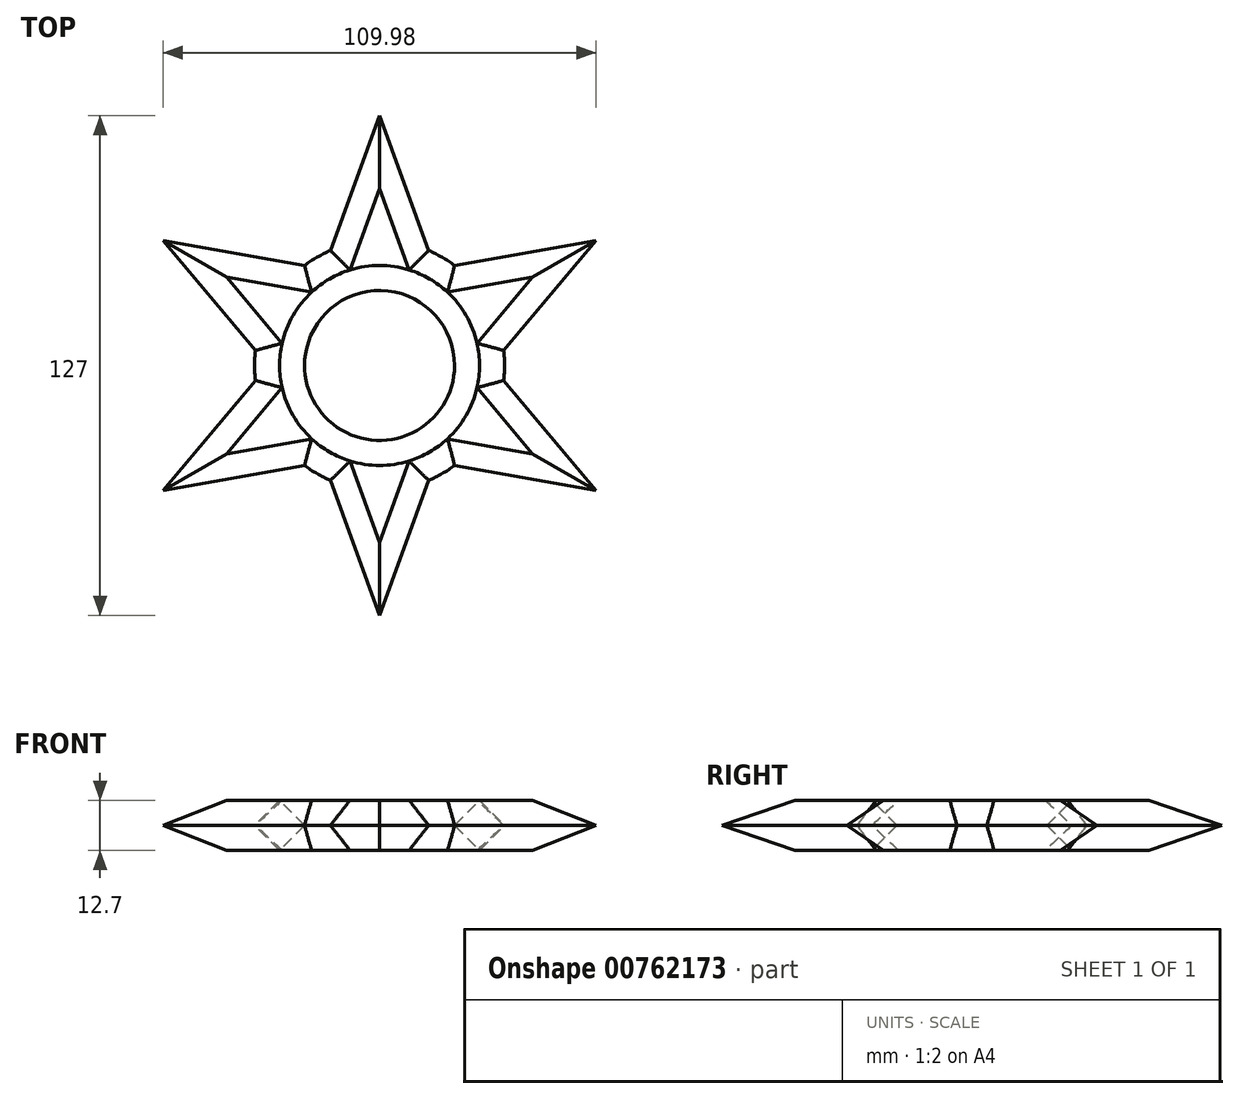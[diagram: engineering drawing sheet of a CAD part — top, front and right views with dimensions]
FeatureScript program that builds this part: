
annotation { "Feature Type Name" : "Feature", "Feature Type Description" : "" }
export const myFeature = defineFeature(function(context is Context, id is Id, definition is map)
    precondition{}
    {
        {
            var Q0;
            Q0=qCreatedBy(makeId("Top.planeOp"),FACE);
            var sketch = newSketch(context, id + "F0", { "sketchPlane" : qUnion([Q0])});
            skCircle(sketch, "E0", {"center": v(0, 0) * mm, "radius": 31.75 * mm});
            skCircle(sketch, "E1", {"center": v(0, 0) * mm, "radius": 19.05 * mm});
            skSolve(sketch);
        }
        {
            var Q0;
            Q0 = qSketchRegion(id + "F0", true);
            extrude(context, id + "F1", {"entities" : qUnion([Q0]), "endBound" : BoundingType.SYMMETRIC, "depth" : 12.7 * mm, "offsetDistance" : 25.4 * mm});
        }
        {
            var Q0;
            Q0=makeQuery(id+"F1.opExtrude","CAP_FACE",FACE,{"disambiguationData":[OSD([sQuery(id+"F0.wireOp",EDGE,"E0"),sQuery(id+"F0.wireOp",EDGE,"E1")])],"isStart":false});
            var sketch = newSketch(context, id + "F2", { "sketchPlane" : qUnion([Q0])});
            skLineSegment(sketch, "E2", {"start": v(0, 0) * mm, "end": v(0, 63.5) * mm});
            skCircle(sketch, "E3.0", {"center": v(0, 0) * mm, "radius": 31.75 * mm});
            skLineSegment(sketch, "E4", {"start": v(0, 63.5) * mm, "end": v(-12.49, 29.2) * mm});
            skLineSegment(sketch, "E5", {"start": v(0, 63.5) * mm, "end": v(12.49, 29.2) * mm});
            skLineSegment(sketch, "E6.1.0", {"start": v(-55, 31.75) * mm, "end": v(-31.52, 3.78) * mm});
            skLineSegment(sketch, "E6.1.1", {"start": v(-55, 31.75) * mm, "end": v(-19.04, 25.4) * mm});
            skLineSegment(sketch, "E6.2.0", {"start": v(-55, -31.75) * mm, "end": v(-19.04, -25.4) * mm});
            skLineSegment(sketch, "E6.2.1", {"start": v(-55, -31.75) * mm, "end": v(-31.52, -3.78) * mm});
            skLineSegment(sketch, "E6.3.0", {"start": v(0, -63.5) * mm, "end": v(12.49, -29.2) * mm});
            skLineSegment(sketch, "E6.3.1", {"start": v(0, -63.5) * mm, "end": v(-12.49, -29.2) * mm});
            skLineSegment(sketch, "E6.4.0", {"start": v(55, -31.75) * mm, "end": v(31.52, -3.78) * mm});
            skLineSegment(sketch, "E6.4.1", {"start": v(55, -31.75) * mm, "end": v(19.04, -25.4) * mm});
            skLineSegment(sketch, "E6.5.0", {"start": v(55, 31.75) * mm, "end": v(19.04, 25.4) * mm});
            skLineSegment(sketch, "E6.5.1", {"start": v(55, 31.75) * mm, "end": v(31.52, 3.78) * mm});
            skSolve(sketch);
        }
        {
            var Q0;
            {var subQ0=sQuery(id+"F2.wireOp",EDGE,"E4");Q0=makeQuery(id+"F2.imprint","IMPRINT",FACE,{"disambiguationData":[TD([[makeQuery(id+"F2.imprint","IMPRINT",EDGE,{"derivedFrom":subQ0}),1.0]])]});}
            var Q1;
            {var subQ0=sQuery(id+"F2.wireOp",EDGE,"E5");Q1=makeQuery(id+"F2.imprint","IMPRINT",FACE,{"disambiguationData":[TD([[makeQuery(id+"F2.imprint","IMPRINT",EDGE,{"derivedFrom":subQ0}),-1.0]])]});}
            var Q2;
            {var subQ0=sQuery(id+"F2.wireOp",EDGE,"E6.5.0");Q2=makeQuery(id+"F2.imprint","IMPRINT",FACE,{"disambiguationData":[TD([[makeQuery(id+"F2.imprint","IMPRINT",EDGE,{"derivedFrom":subQ0}),1.0]])]});}
            var Q3;
            {var subQ0=sQuery(id+"F2.wireOp",EDGE,"E6.1.0");Q3=makeQuery(id+"F2.imprint","IMPRINT",FACE,{"disambiguationData":[TD([[makeQuery(id+"F2.imprint","IMPRINT",EDGE,{"derivedFrom":subQ0}),1.0]])]});}
            var Q4;
            {var subQ0=sQuery(id+"F2.wireOp",EDGE,"E6.2.0");Q4=makeQuery(id+"F2.imprint","IMPRINT",FACE,{"disambiguationData":[TD([[makeQuery(id+"F2.imprint","IMPRINT",EDGE,{"derivedFrom":subQ0}),1.0]])]});}
            var Q5;
            {var subQ0=sQuery(id+"F2.wireOp",EDGE,"E6.4.0");Q5=makeQuery(id+"F2.imprint","IMPRINT",FACE,{"disambiguationData":[TD([[makeQuery(id+"F2.imprint","IMPRINT",EDGE,{"derivedFrom":subQ0}),1.0]])]});}
            var Q6;
            {var subQ0=sQuery(id+"F2.wireOp",EDGE,"E6.3.0");Q6=makeQuery(id+"F2.imprint","IMPRINT",FACE,{"disambiguationData":[TD([[makeQuery(id+"F2.imprint","IMPRINT",EDGE,{"derivedFrom":subQ0}),1.0]])]});}
            extrude(context, id + "F3", {"entities" : qUnion([Q0, Q1, Q2, Q3, Q4, Q5, Q6]), "operationType" : NewBodyOperationType.ADD, "oppositeDirection" : true, "depth" : 12.7 * mm, "offsetDistance" : 25.4 * mm});
        }
        {
            var Q0;
            {var subQ0=sQuery(id+"F2.wireOp",EDGE,"E3.0");Q0=makeQuery(id+"F3.boolean.opBoolean","MERGE",FACE,{"derivedFrom":[makeQuery(id+"F1.opExtrude","CAP_FACE",FACE,{"disambiguationData":[OSD([sQuery(id+"F0.wireOp",EDGE,"E0"),sQuery(id+"F0.wireOp",EDGE,"E1")])],"isStart":false}),makeQuery(id+"F3.opExtrude","CAP_FACE",FACE,{"disambiguationData":[OSD([subQ0,sQuery(id+"F2.wireOp",EDGE,"E6.5.0"),sQuery(id+"F2.wireOp",EDGE,"E6.5.1")])],"isStart":true}),makeQuery(id+"F3.opExtrude","CAP_FACE",FACE,{"disambiguationData":[OSD([subQ0,sQuery(id+"F2.wireOp",EDGE,"E4"),sQuery(id+"F2.wireOp",EDGE,"E5")])],"isStart":true}),makeQuery(id+"F3.opExtrude","CAP_FACE",FACE,{"disambiguationData":[OSD([subQ0,sQuery(id+"F2.wireOp",EDGE,"E6.1.0"),sQuery(id+"F2.wireOp",EDGE,"E6.1.1")])],"isStart":true}),makeQuery(id+"F3.opExtrude","CAP_FACE",FACE,{"disambiguationData":[OSD([subQ0,sQuery(id+"F2.wireOp",EDGE,"E6.2.0"),sQuery(id+"F2.wireOp",EDGE,"E6.2.1")])],"isStart":true}),makeQuery(id+"F3.opExtrude","CAP_FACE",FACE,{"disambiguationData":[OSD([subQ0,sQuery(id+"F2.wireOp",EDGE,"E6.3.0"),sQuery(id+"F2.wireOp",EDGE,"E6.3.1")])],"isStart":true}),makeQuery(id+"F3.opExtrude","CAP_FACE",FACE,{"disambiguationData":[OSD([subQ0,sQuery(id+"F2.wireOp",EDGE,"E6.4.0"),sQuery(id+"F2.wireOp",EDGE,"E6.4.1")])],"isStart":true})]});}
            var Q1;
            {var subQ0=sQuery(id+"F2.wireOp",EDGE,"E3.0");Q1=makeQuery(id+"F3.boolean.opBoolean","MERGE",FACE,{"derivedFrom":[makeQuery(id+"F1.opExtrude","CAP_FACE",FACE,{"disambiguationData":[OSD([sQuery(id+"F0.wireOp",EDGE,"E0"),sQuery(id+"F0.wireOp",EDGE,"E1")])],"isStart":true}),makeQuery(id+"F3.opExtrude","CAP_FACE",FACE,{"disambiguationData":[OSD([subQ0,sQuery(id+"F2.wireOp",EDGE,"E6.5.0"),sQuery(id+"F2.wireOp",EDGE,"E6.5.1")])],"isStart":false}),makeQuery(id+"F3.opExtrude","CAP_FACE",FACE,{"disambiguationData":[OSD([subQ0,sQuery(id+"F2.wireOp",EDGE,"E4"),sQuery(id+"F2.wireOp",EDGE,"E5")])],"isStart":false}),makeQuery(id+"F3.opExtrude","CAP_FACE",FACE,{"disambiguationData":[OSD([subQ0,sQuery(id+"F2.wireOp",EDGE,"E6.1.0"),sQuery(id+"F2.wireOp",EDGE,"E6.1.1")])],"isStart":false}),makeQuery(id+"F3.opExtrude","CAP_FACE",FACE,{"disambiguationData":[OSD([subQ0,sQuery(id+"F2.wireOp",EDGE,"E6.2.0"),sQuery(id+"F2.wireOp",EDGE,"E6.2.1")])],"isStart":false}),makeQuery(id+"F3.opExtrude","CAP_FACE",FACE,{"disambiguationData":[OSD([subQ0,sQuery(id+"F2.wireOp",EDGE,"E6.3.0"),sQuery(id+"F2.wireOp",EDGE,"E6.3.1")])],"isStart":false}),makeQuery(id+"F3.opExtrude","CAP_FACE",FACE,{"disambiguationData":[OSD([subQ0,sQuery(id+"F2.wireOp",EDGE,"E6.4.0"),sQuery(id+"F2.wireOp",EDGE,"E6.4.1")])],"isStart":false})]});}
            chamfer(context, id + "F4", {"entities" : qUnion([Q0, Q1]), "width" : 6.35 * mm, "tangentPropagation" : true});
        }
    });
